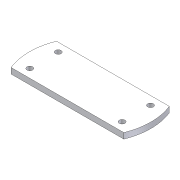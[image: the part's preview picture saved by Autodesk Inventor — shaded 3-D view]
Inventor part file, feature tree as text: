
AUTODESK INVENTOR PART (.ipt)
format: ipt  version: unknown  size: 167,936 bytes
history: native  units: mm
features: extrude x1, sketch x1
ambient origin geometry x8: Origin, YZ Plane, XZ Plane, XY Plane, X Axis, Y Axis, Z Axis, Center Point
feature tree (2):
  extrude  "Extrusion1"  Depth=214.0mm
  sketch  "Sketch1"  dims[d0=194.0mm d1=214.0mm d2=80.0mm d3=170.0mm d4=25.0mm d5=10.0mm d6=107.0mm d7=107.0mm d8=10.0mm d9=0.0mm]
